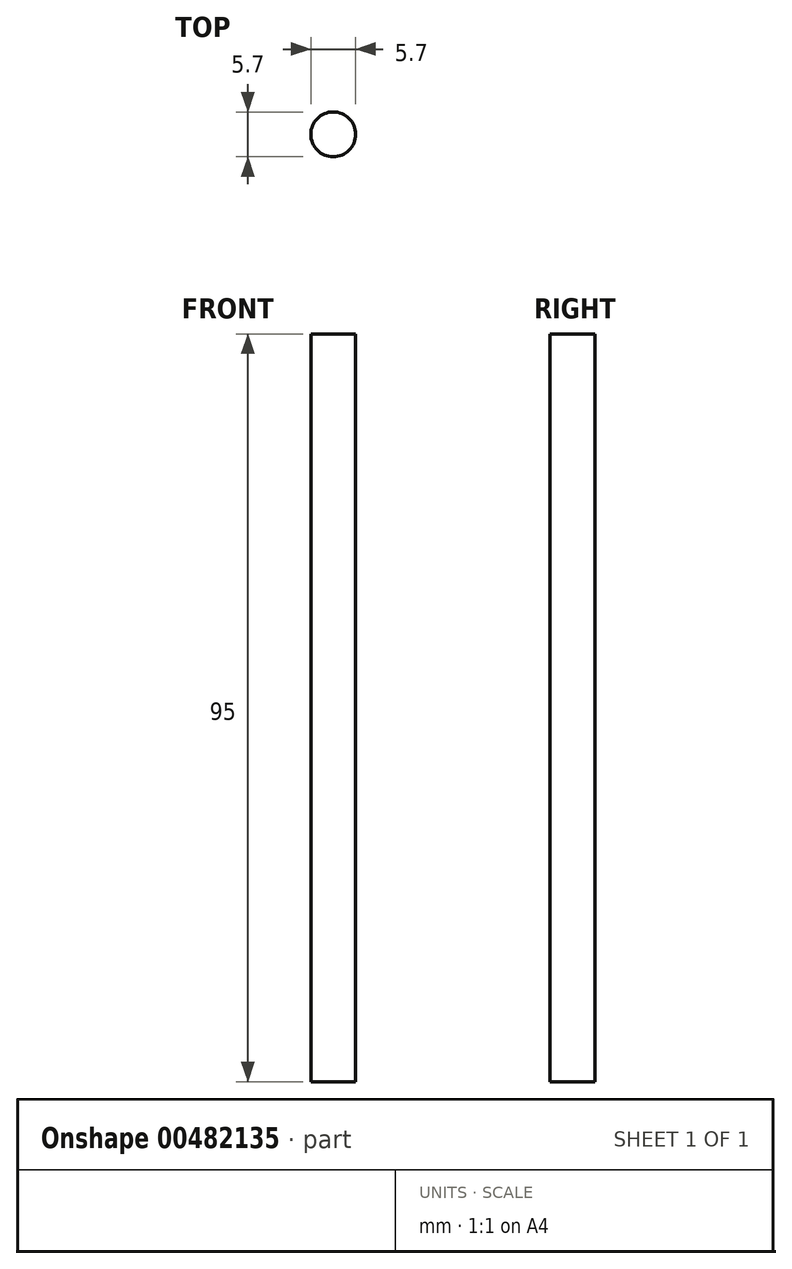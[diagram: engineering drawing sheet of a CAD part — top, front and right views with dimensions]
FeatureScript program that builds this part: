
annotation { "Feature Type Name" : "Feature", "Feature Type Description" : "" }
export const myFeature = defineFeature(function(context is Context, id is Id, definition is map)
    precondition{}
    {
        {
            var Q0;
            Q0=qCreatedBy(makeId("Top.planeOp"),FACE);
            var sketch = newSketch(context, id + "F0", { "sketchPlane" : qUnion([Q0])});
            skCircle(sketch, "E0", {"center": v(0, 0) * mm, "radius": 2.85 * mm});
            skSolve(sketch);
        }
        {
            var Q0;
            Q0=makeQuery(id+"F0.imprint","IMPRINT",FACE,{"disambiguationData":[TD([[makeQuery(id+"F0.imprint","IMPRINT",EDGE,{"derivedFrom":sQuery(id+"F0.wireOp",EDGE,"E0")}),1.0]])]});
            extrude(context, id + "F1", {"entities" : qUnion([Q0]), "depth" : 95 * mm});
        }
    });
